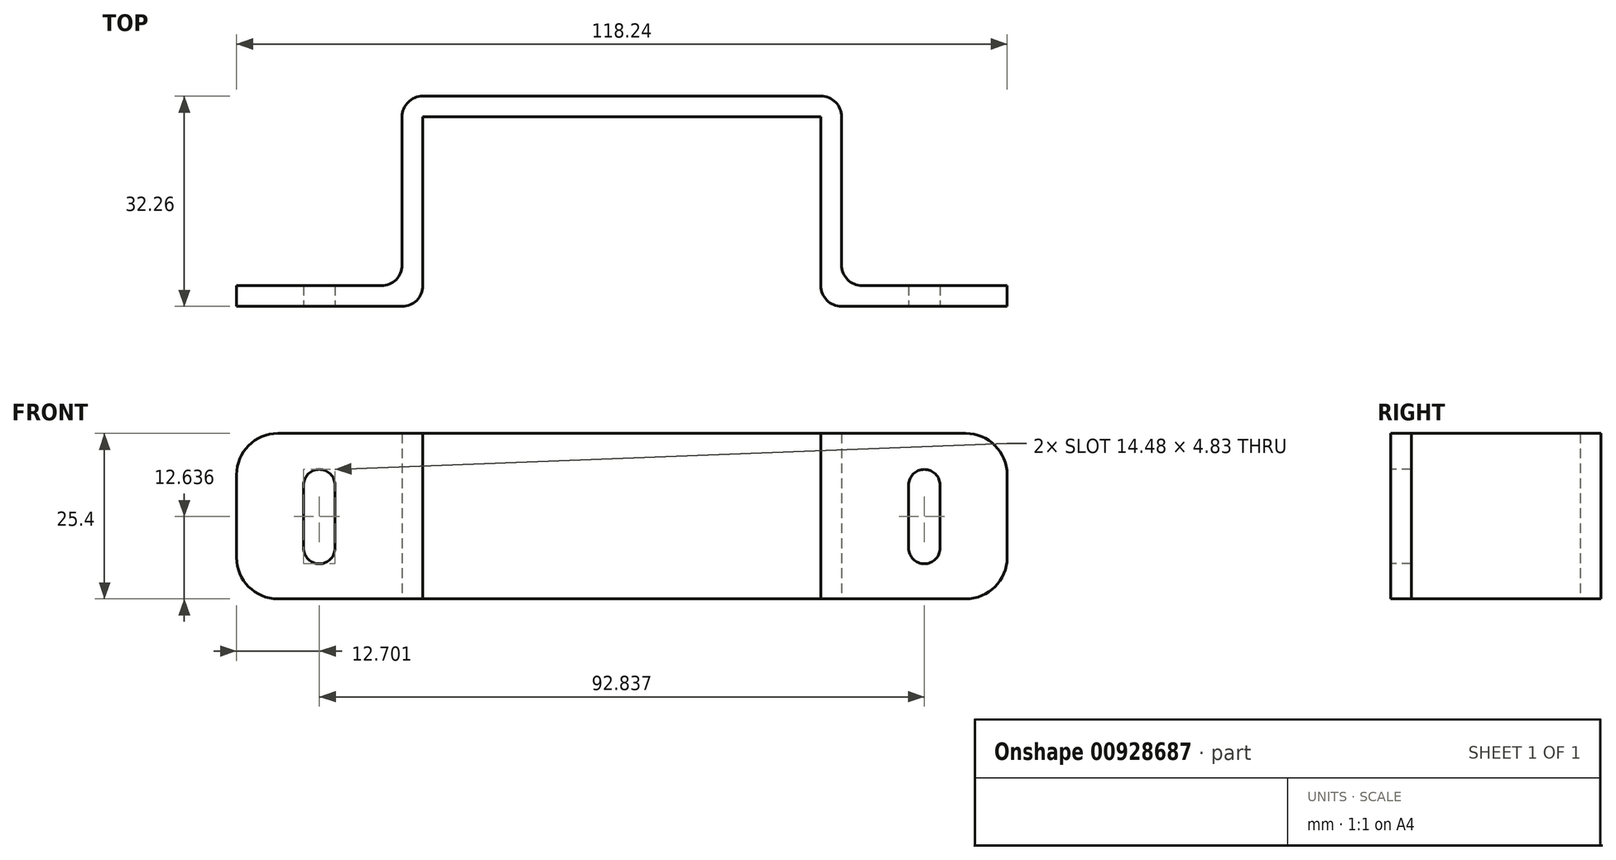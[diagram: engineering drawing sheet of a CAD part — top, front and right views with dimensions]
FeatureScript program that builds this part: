
annotation { "Feature Type Name" : "Feature", "Feature Type Description" : "" }
export const myFeature = defineFeature(function(context is Context, id is Id, definition is map)
    precondition{}
    {
        {
            var Q0;
            Q0=qCreatedBy(makeId("Top.planeOp"),FACE);
            var sketch = newSketch(context, id + "F0", { "sketchPlane" : qUnion([Q0])});
            skLineSegment(sketch, "E0", {"start": v(0, 29.08) * mm, "end": v(30.54, 29.08) * mm});
            skLineSegment(sketch, "E1", {"start": v(30.54, 29.08) * mm, "end": v(30.54, 0) * mm});
            skLineSegment(sketch, "E2", {"start": v(30.54, 0) * mm, "end": v(59.12, 0) * mm});
            skLineSegment(sketch, "E3.0", {"start": v(33.72, 3.17) * mm, "end": v(59.12, 3.17) * mm});
            skLineSegment(sketch, "E3.1", {"start": v(33.72, 32.26) * mm, "end": v(33.72, 3.18) * mm});
            skLineSegment(sketch, "E3.2", {"start": v(0, 32.26) * mm, "end": v(33.72, 32.26) * mm});
            skLineSegment(sketch, "E4", {"start": v(59.12, 3.18) * mm, "end": v(59.12, 0) * mm});
            skLineSegment(sketch, "E5.MirrorCS", {"start": v(-59.12, 3.18) * mm, "end": v(-59.12, 0) * mm});
            skLineSegment(sketch, "E6.MirrorCS", {"start": v(-30.54, 29.08) * mm, "end": v(-30.54, 0) * mm});
            skLineSegment(sketch, "E7.MirrorCS", {"start": v(0, 32.26) * mm, "end": v(-33.72, 32.26) * mm});
            skLineSegment(sketch, "E8.MirrorCS", {"start": v(-33.72, 3.17) * mm, "end": v(-59.12, 3.17) * mm});
            skLineSegment(sketch, "E9.MirrorCS", {"start": v(-30.54, 0) * mm, "end": v(-59.12, 0) * mm});
            skLineSegment(sketch, "E10.MirrorCS", {"start": v(0, 29.08) * mm, "end": v(-30.54, 29.08) * mm});
            skLineSegment(sketch, "E11.MirrorCS", {"start": v(-33.72, 32.26) * mm, "end": v(-33.72, 3.18) * mm});
            skSolve(sketch);
        }
        {
            var Q0;
            Q0=qSketchRegion(id+"F0",true);
            extrude(context, id + "F1", {"entities" : qUnion([Q0]), "depth" : 25.4 * mm, "offsetDistance" : 25.4 * mm});
        }
        {
            var Q0;
            Q0=makeQuery(id+"F1.opExtrude","SWEPT_EDGE",EDGE,{"disambiguationData":[OSD([sQuery(id+"F0.wireOp",EDGE,"E6.MirrorCS"),sQuery(id+"F0.wireOp",EDGE,"E9.MirrorCS")])]});
            var Q1;
            Q1=makeQuery(id+"F1.opExtrude","SWEPT_EDGE",EDGE,{"disambiguationData":[OSD([sQuery(id+"F0.wireOp",EDGE,"E1"),sQuery(id+"F0.wireOp",EDGE,"E2")])]});
            fillet(context, id + "F2", {"entities" : qUnion([Q0, Q1]), "radius" : 3.17 * mm, "tangentPropagation" : true, "allowEdgeOverflow" : false});
        }
        {
            var Q0;
            Q0=qCreatedBy(makeId("Front.planeOp"),FACE);
            var sketch = newSketch(context, id + "F3", { "sketchPlane" : qUnion([Q0])});
            skLineSegment(sketch, "E12", {"start": v(-46.42, 7.81) * mm, "end": v(-46.42, 17.46) * mm});
            skArc(sketch, "E13.0.startCap", {"start": v(-44, 7.81) * mm, "mid": v(-46.42, 5.4) * mm, "end": v(-48.83, 7.81) * mm});
            skArc(sketch, "E13.0.endCap", {"start": v(-48.83, 17.46) * mm, "mid": v(-46.42, 19.88) * mm, "end": v(-44, 17.46) * mm});
            skLineSegment(sketch, "E13.0.left", {"start": v(-48.83, 7.81) * mm, "end": v(-48.83, 17.46) * mm});
            skLineSegment(sketch, "E13.0.right", {"start": v(-44, 7.81) * mm, "end": v(-44, 17.46) * mm});
            skLineSegment(sketch, "E14.MirrorCS", {"start": v(44, 7.81) * mm, "end": v(44, 17.46) * mm});
            skLineSegment(sketch, "E15.MirrorCS", {"start": v(46.42, 7.81) * mm, "end": v(46.42, 17.46) * mm});
            skLineSegment(sketch, "E16.MirrorCS", {"start": v(48.83, 7.81) * mm, "end": v(48.83, 17.46) * mm});
            skArc(sketch, "E17.MirrorCS", {"start": v(48.83, 17.46) * mm, "mid": v(46.42, 19.88) * mm, "end": v(44, 17.46) * mm});
            skArc(sketch, "E18.MirrorCS", {"start": v(44, 7.81) * mm, "mid": v(46.42, 5.4) * mm, "end": v(48.83, 7.81) * mm});
            skSolve(sketch);
        }
        {
            var Q0;
            Q0=qSketchRegion(id+"F3",true);
            extrude(context, id + "F4", {"entities" : qUnion([Q0]), "operationType" : NewBodyOperationType.REMOVE, "endBound" : BoundingType.THROUGH_ALL, "oppositeDirection" : true, "depth" : 25.4 * mm, "offsetDistance" : 25.4 * mm});
        }
        {
            var Q0;
            Q0=makeQuery(id+"F1.opExtrude","CAP_EDGE",EDGE,{"disambiguationData":[OSD([sQuery(id+"F0.wireOp",EDGE,"E5.MirrorCS")])],"isStart":true});
            var Q1;
            Q1=makeQuery(id+"F1.opExtrude","CAP_EDGE",EDGE,{"disambiguationData":[OSD([sQuery(id+"F0.wireOp",EDGE,"E5.MirrorCS")])],"isStart":false});
            var Q2;
            Q2=makeQuery(id+"F1.opExtrude","CAP_EDGE",EDGE,{"disambiguationData":[OSD([sQuery(id+"F0.wireOp",EDGE,"E4")])],"isStart":false});
            var Q3;
            Q3=makeQuery(id+"F1.opExtrude","CAP_EDGE",EDGE,{"disambiguationData":[OSD([sQuery(id+"F0.wireOp",EDGE,"E4")])],"isStart":true});
            fillet(context, id + "F5", {"entities" : qUnion([Q0, Q1, Q2, Q3]), "radius" : 6.35 * mm, "tangentPropagation" : true, "allowEdgeOverflow" : false});
        }
        {
            var Q0;
            Q0=makeQuery(id+"F1.opExtrude","SWEPT_EDGE",EDGE,{"disambiguationData":[OSD([sQuery(id+"F0.wireOp",EDGE,"E8.MirrorCS"),sQuery(id+"F0.wireOp",EDGE,"E11.MirrorCS")])]});
            var Q1;
            Q1=makeQuery(id+"F1.opExtrude","SWEPT_EDGE",EDGE,{"disambiguationData":[OSD([sQuery(id+"F0.wireOp",EDGE,"E7.MirrorCS"),sQuery(id+"F0.wireOp",EDGE,"E11.MirrorCS")])]});
            var Q2;
            Q2=makeQuery(id+"F1.opExtrude","SWEPT_EDGE",EDGE,{"disambiguationData":[OSD([sQuery(id+"F0.wireOp",EDGE,"E3.1"),sQuery(id+"F0.wireOp",EDGE,"E3.2")])]});
            var Q3;
            Q3=makeQuery(id+"F1.opExtrude","SWEPT_EDGE",EDGE,{"disambiguationData":[OSD([sQuery(id+"F0.wireOp",EDGE,"E3.0"),sQuery(id+"F0.wireOp",EDGE,"E3.1")])]});
            fillet(context, id + "F6", {"entities" : qUnion([Q0, Q1, Q2, Q3]), "radius" : 3.17 * mm, "tangentPropagation" : true, "allowEdgeOverflow" : false});
        }
    });
